# Revit family: 304_Cim771 HF-_
name_source: partatom
category: Pipe Accessories
units: mm (PartAtom-declared; Revit-internal decimal feet)

## family parameters
Always vertical = Yes
Cut with Voids When Loaded = No
Part Type = Valve - Breaks Into
Round Connector Dimension = Use Diameter
Shared = No
Work Plane-Based = No

## types (6) — shared parameters
B1 = 125 mm
BB2 = 63 mm
CAT0 = Yes
DD1 = 8 mm  [stored 0.0262467 ft]
DD2 = 5 mm  [stored 0.0164042 ft]
DD3 = 16 mm  [stored 0.0524934 ft]
DD4 = 65 mm
DD5 = 29 mm  [stored 0.0951444 ft]
Description = ELECTRONIC DIFFERENTIAL PRESSURE CONTROL VALVE - PN 16 - "CR" BRASS
HH2 = 16 mm  [stored 0.0524934 ft]
HH3 = 4 mm  [stored 0.0131234 ft]
L2D_Min = 3048 mm
LL5 = 6 mm  [stored 0.019685 ft]
Manufacturer = Cimberio
QmdConnectorList = 301;D;302;D
URL = www.cimberio.it
WW1 = 8 mm  [stored 0.0262467 ft]
WW2 = 4 mm  [stored 0.0131234 ft]
WW3 = 39 mm  [stored 0.127953 ft]
magiPartTypeId = 304
magiProductFamilyId = Cim771 HF-*
zero-valued in all types: MC_Default_elevation

## per-type parameters (varying)
| type | BB1 | CenSd_R1_6 | D | HH1 | HH4 | HH5 | HH6 | HH7 | HH8 | L2D | LL1 | LL2 | LL2__ve | LL3 | LL4 | LL6 | R | R1 | W2D | magiProductId |
| Cim771-15 (0-1000 mbar) | 47 mm | 11 mm | 15 mm | 29 mm  [stored 0.0951444 ft] | 48 mm | 12 mm  [stored 0.0393701 ft] | 9 mm  [stored 0.0295276 ft] | 65 mm | 12 mm  [stored 0.0393701 ft] | 128 mm | 64 mm | 17 mm | -17 mm  [stored -0.0557743 ft] | 95 mm | 25 mm  [stored 0.082021 ft] | 35 mm | 8 mm  [stored 0.0262467 ft] | 13 mm | 15 mm  [stored 0.0492126 ft] | Cim771 HF-15 |
| Cim771-50 (0-1000 mbar) | 70 mm | 30 mm  [stored 0.0984252 ft] | 50 mm | 46 mm | 73 mm | 13 mm | 10 mm  [stored 0.0328084 ft] | 71 mm | 13 mm | 183 mm | 92 mm | 24 mm | -24 mm | 136 mm | 36 mm | 50 mm | 25 mm  [stored 0.082021 ft] | 35 mm | 50 mm | Cim771 HF-50 |
| Cim771-40 (0-1000 mbar) | 59 mm | 24 mm | 40 mm | 41 mm | 66 mm | 13 mm | 10 mm  [stored 0.0328084 ft] | 71 mm | 13 mm | 162 mm | 81 mm | 21 mm | -21 mm | 120 mm | 32 mm  [stored 0.104987 ft] | 44 mm | 20 mm  [stored 0.0656168 ft] | 28 mm | 40 mm | Cim771 HF-40 |
| Cim771-32 (0-1000 mbar) | 53 mm | 21 mm | 32 mm | 37 mm | 61 mm | 12 mm  [stored 0.0393701 ft] | 9 mm  [stored 0.0295276 ft] | 67 mm | 12 mm  [stored 0.0393701 ft] | 150 mm | 75 mm | 19 mm | -19 mm | 111 mm | 30 mm  [stored 0.0984252 ft] | 41 mm | 16 mm  [stored 0.0524934 ft] | 25 mm  [stored 0.082021 ft] | 32 mm  [stored 0.104987 ft] | Cim771 HF-32 |
| Cim771-25 (0-1000 mbar) | 47 mm | 17 mm | 25 mm | 34 mm | 55 mm | 12 mm  [stored 0.0393701 ft] | 9 mm  [stored 0.0295276 ft] | 65 mm | 12 mm  [stored 0.0393701 ft] | 139 mm | 70 mm | 18 mm | -18 mm | 103 mm | 28 mm | 38 mm | 13 mm | 20 mm  [stored 0.0656168 ft] | 25 mm  [stored 0.082021 ft] | Cim771 HF-25 |
| Cim771-20 (0-1000 mbar) | 47 mm | 11 mm | 20 mm | 31 mm | 48 mm | 12 mm  [stored 0.0393701 ft] | 9 mm  [stored 0.0295276 ft] | 65 mm | 12 mm  [stored 0.0393701 ft] | 132 mm | 66 mm | 17 mm | -17 mm  [stored -0.0557743 ft] | 98 mm | 26 mm | 36 mm | 10 mm  [stored 0.0328084 ft] | 13 mm | 20 mm  [stored 0.0656168 ft] | Cim771 HF-20 |

note: column(s) folded — value = type name in every type: magiProductCode

note: [stored X ft] marks values corroborated as IEEE doubles in the binary element streams (Revit-internal decimal feet)

## geometry (parser evidence)
native form markers: Sweep x2
no freeform markers — native parametric forms only
